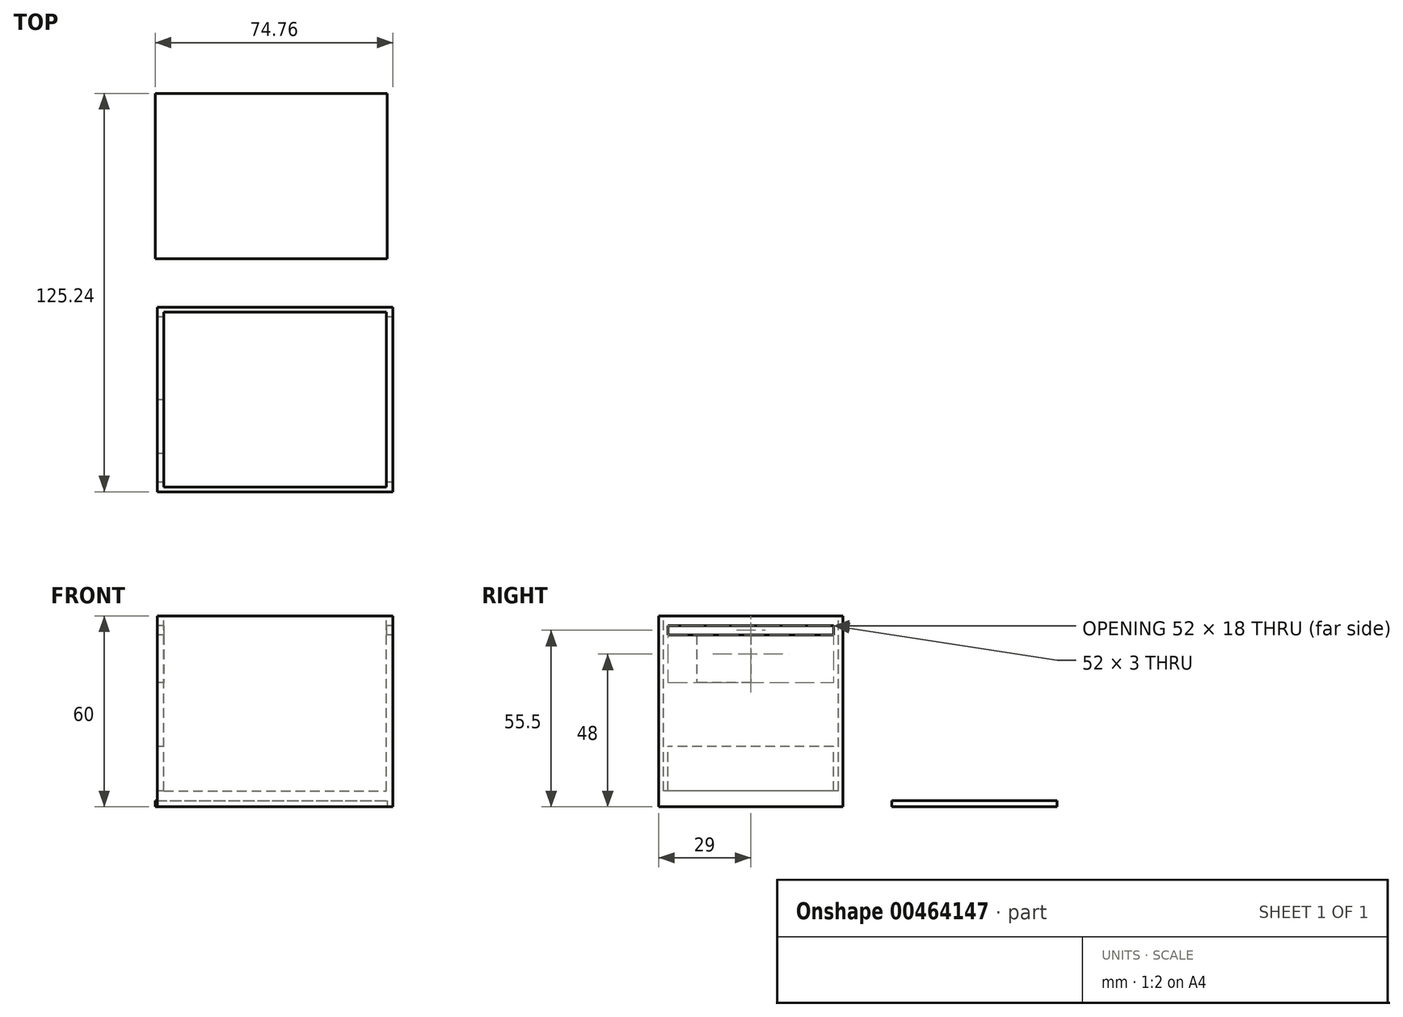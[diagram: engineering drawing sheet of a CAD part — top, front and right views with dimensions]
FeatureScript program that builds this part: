
annotation { "Feature Type Name" : "Feature", "Feature Type Description" : "" }
export const myFeature = defineFeature(function(context is Context, id is Id, definition is map)
    precondition{}
    {
        {
            var Q0;
            Q0=qCreatedBy(makeId("Top.planeOp"),FACE);
            var sketch = newSketch(context, id + "F0", { "sketchPlane" : qUnion([Q0])});
            skLineSegment(sketch, "E0.bottom", {"start": v(-37, 29) * mm, "end": v(37, 29) * mm});
            skLineSegment(sketch, "E0.top", {"start": v(-37, -29) * mm, "end": v(37, -29) * mm});
            skLineSegment(sketch, "E0.left", {"start": v(-37, 29) * mm, "end": v(-37, -29) * mm});
            skLineSegment(sketch, "E0.right", {"start": v(37, 29) * mm, "end": v(37, -29) * mm});
            skLineSegment(sketch, "E1", {"start": v(-37, 0) * mm, "end": v(0, 0) * mm});
            skPoint(sketch, "E1.startSnap0", {"position": v(-37, 0) * mm});
            skLineSegment(sketch, "E2", {"start": v(0, 0) * mm, "end": v(37, 0) * mm});
            skLineSegment(sketch, "E3", {"start": v(0, 29) * mm, "end": v(0, 0) * mm});
            skLineSegment(sketch, "E4", {"start": v(0, 0) * mm, "end": v(0, -29) * mm});
            skSolve(sketch);
        }
        {
            var Q0;
            Q0 = qSketchRegion(id + "F0", true);
            extrude(context, id + "F1", {"entities" : qUnion([Q0]), "depth" : 60 * mm});
        }
        {
            var Q0;
            Q0=makeQuery(id+"F1.opExtrude","CAP_FACE",FACE,{"disambiguationData":[OSD([sQuery(id+"F0.wireOp",EDGE,"E0.bottom"),sQuery(id+"F0.wireOp",EDGE,"E0.top"),sQuery(id+"F0.wireOp",EDGE,"E0.left"),sQuery(id+"F0.wireOp",EDGE,"E0.right")])],"isStart":false});
            var sketch = newSketch(context, id + "F2", { "sketchPlane" : qUnion([Q0])});
            skLineSegment(sketch, "E5.bottom", {"start": v(-35, 27.5) * mm, "end": v(35, 27.5) * mm});
            skLineSegment(sketch, "E5.top", {"start": v(-35, -27.5) * mm, "end": v(35, -27.5) * mm});
            skLineSegment(sketch, "E5.left", {"start": v(-35, 27.5) * mm, "end": v(-35, -27.5) * mm});
            skLineSegment(sketch, "E5.right", {"start": v(35, 27.5) * mm, "end": v(35, -27.5) * mm});
            skLineSegment(sketch, "E6", {"start": v(0, 0) * mm, "end": v(0, 27.5) * mm});
            skLineSegment(sketch, "E7", {"start": v(0, 0) * mm, "end": v(0, -27.5) * mm});
            skLineSegment(sketch, "E8", {"start": v(0, 0) * mm, "end": v(35, 0) * mm});
            skLineSegment(sketch, "E9", {"start": v(0, 0) * mm, "end": v(-35, 0) * mm});
            skSolve(sketch);
        }
        {
            var Q0;
            Q0 = qSketchRegion(id + "F2", true);
            extrude(context, id + "F3", {"entities" : qUnion([Q0]), "operationType" : NewBodyOperationType.REMOVE, "oppositeDirection" : true, "depth" : 55 * mm});
        }
        {
            var Q0;
            Q0=makeQuery(id+"F1.opExtrude","SWEPT_FACE",FACE,{"disambiguationData":[OSD([sQuery(id+"F0.wireOp",EDGE,"E0.left")])]});
            var sketch = newSketch(context, id + "F4", { "sketchPlane" : qUnion([Q0])});
            skLineSegment(sketch, "E10.bottom", {"start": v(-26, 5) * mm, "end": v(26, 5) * mm});
            skLineSegment(sketch, "E10.top", {"start": v(-26, 19) * mm, "end": v(26, 19) * mm});
            skLineSegment(sketch, "E10.left", {"start": v(-26, 5) * mm, "end": v(-26, 19) * mm});
            skLineSegment(sketch, "E10.right", {"start": v(26, 5) * mm, "end": v(26, 19) * mm});
            skLineSegment(sketch, "E11", {"start": v(-26, 12) * mm, "end": v(0, 12) * mm});
            skLineSegment(sketch, "E12", {"start": v(26, 12) * mm, "end": v(0, 12) * mm});
            skSolve(sketch);
        }
        {
            var Q0;
            Q0 = qSketchRegion(id + "F4", true);
            extrude(context, id + "F5", {"entities" : qUnion([Q0]), "operationType" : NewBodyOperationType.REMOVE, "oppositeDirection" : true, "depth" : 3 * mm});
        }
        {
            var Q0;
            Q0=makeQuery(id+"F1.opExtrude","SWEPT_FACE",FACE,{"disambiguationData":[OSD([sQuery(id+"F0.wireOp",EDGE,"E0.left")])]});
            var sketch = newSketch(context, id + "F6", { "sketchPlane" : qUnion([Q0])});
            skLineSegment(sketch, "E13.bottom", {"start": v(0, 54) * mm, "end": v(17, 54) * mm});
            skLineSegment(sketch, "E13.top", {"start": v(0, 39) * mm, "end": v(17, 39) * mm});
            skLineSegment(sketch, "E13.left", {"start": v(0, 54) * mm, "end": v(0, 39) * mm});
            skLineSegment(sketch, "E13.right", {"start": v(17, 54) * mm, "end": v(17, 39) * mm});
            skSolve(sketch);
        }
        {
            var Q0;
            Q0 = qSketchRegion(id + "F6", true);
            extrude(context, id + "F7", {"entities" : qUnion([Q0]), "operationType" : NewBodyOperationType.REMOVE, "oppositeDirection" : true, "depth" : 3 * mm});
        }
        {
            var Q0;
            Q0=makeQuery(id+"F1.opExtrude","SWEPT_FACE",FACE,{"disambiguationData":[OSD([sQuery(id+"F0.wireOp",EDGE,"E0.left")])]});
            var sketch = newSketch(context, id + "F8", { "sketchPlane" : qUnion([Q0])});
            skLineSegment(sketch, "E14.bottom", {"start": v(-26, 57) * mm, "end": v(26, 57) * mm});
            skLineSegment(sketch, "E14.top", {"start": v(-26, 54) * mm, "end": v(26, 54) * mm});
            skLineSegment(sketch, "E14.left", {"start": v(-26, 57) * mm, "end": v(-26, 54) * mm});
            skLineSegment(sketch, "E14.right", {"start": v(26, 57) * mm, "end": v(26, 54) * mm});
            skSolve(sketch);
        }
        {
            var Q0;
            Q0 = qSketchRegion(id + "F8", true);
            extrude(context, id + "F9", {"entities" : qUnion([Q0]), "operationType" : NewBodyOperationType.REMOVE, "oppositeDirection" : true, "depth" : 76.7 * mm});
        }
        {
            var Q0;
            Q0=qCreatedBy(makeId("Top.planeOp"),FACE);
            var sketch = newSketch(context, id + "F10", { "sketchPlane" : qUnion([Q0])});
            skLineSegment(sketch, "E15.bottom", {"start": v(-37.76, 96.24) * mm, "end": v(35.24, 96.24) * mm});
            skLineSegment(sketch, "E15.top", {"start": v(-37.76, 44.24) * mm, "end": v(35.24, 44.24) * mm});
            skLineSegment(sketch, "E15.left", {"start": v(-37.76, 96.24) * mm, "end": v(-37.76, 44.24) * mm});
            skLineSegment(sketch, "E15.right", {"start": v(35.24, 96.24) * mm, "end": v(35.24, 44.24) * mm});
            skSolve(sketch);
        }
        {
            var Q0;
            Q0 = qSketchRegion(id + "F10", true);
            extrude(context, id + "F11", {"entities" : qUnion([Q0]), "depth" : 2 * mm});
        }
    });
